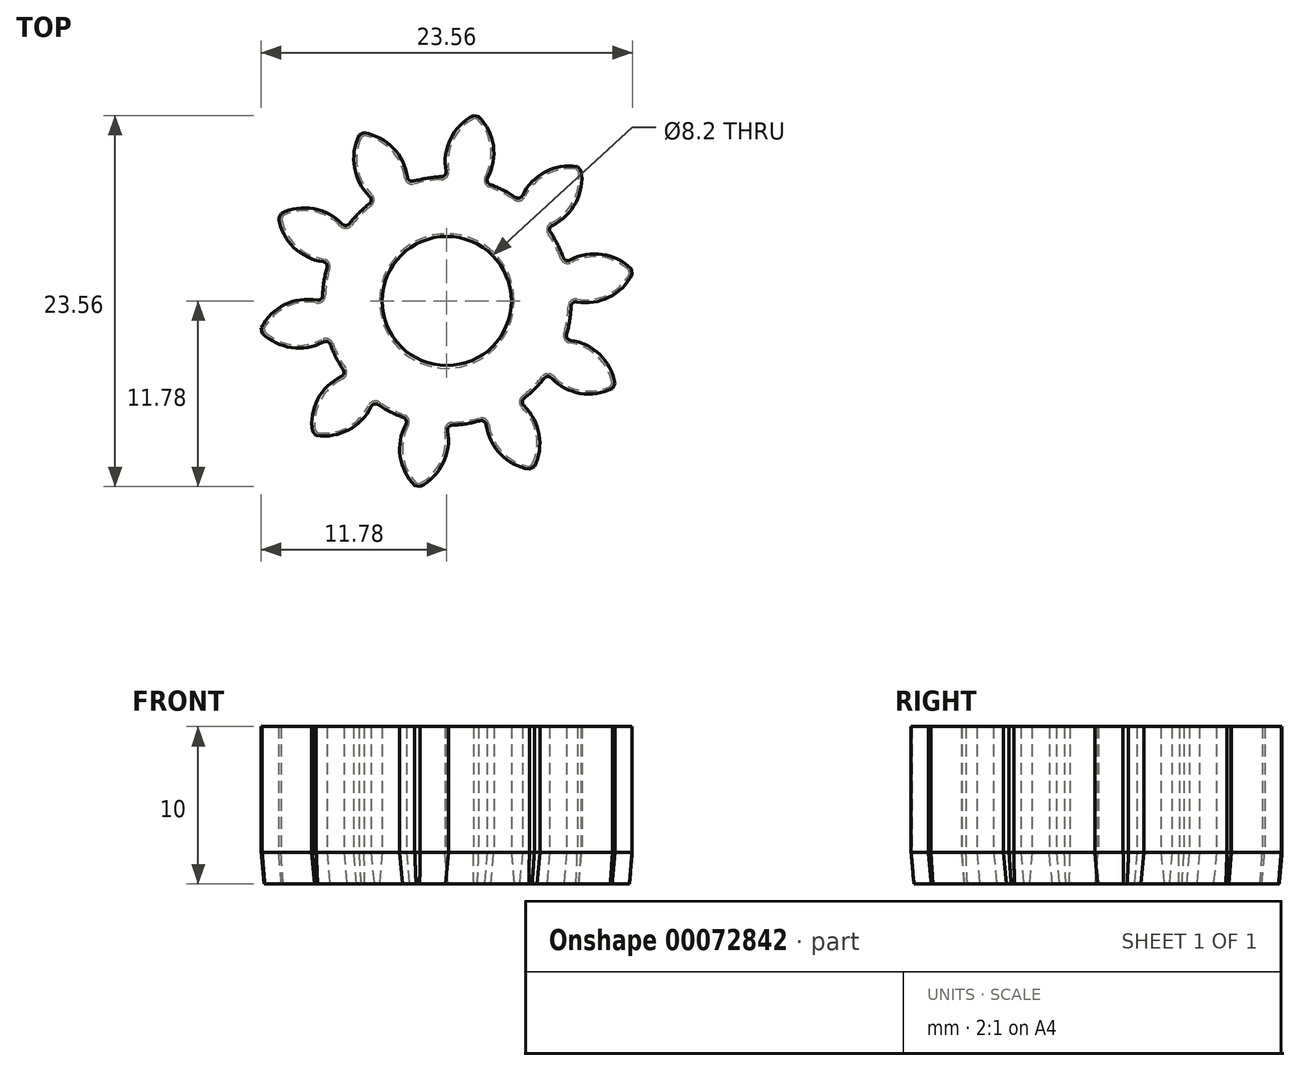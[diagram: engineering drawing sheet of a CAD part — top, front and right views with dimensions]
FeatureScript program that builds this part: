
annotation { "Feature Type Name" : "Feature", "Feature Type Description" : "" }
export const myFeature = defineFeature(function(context is Context, id is Id, definition is map)
    precondition{}
    {
        {
            assignVariable(context, id + "F0", {"name" : "z", "anyValue" : 10});
        }
        {
            assignVariable(context, id + "F1", {"name" : "b1", "anyValue" : 8});
        }
        {
            assignVariable(context, id + "F2", {"name" : "b2", "anyValue" : 2});
        }
        {
            var Q0;
            Q0=qCreatedBy(makeId("Top.planeOp"),FACE);
            var sketch = newSketch(context, id + "F3", { "sketchPlane" : qUnion([Q0])});
            skCircle(sketch, "E0", {"center": v(0, 0) * mm, "radius": 12 * mm, "construction": true});
            skCircle(sketch, "E1", {"center": v(0, 0) * mm, "radius": 9.4 * mm, "construction": true});
            skCircle(sketch, "E2", {"center": v(0, 0) * mm, "radius": 10 * mm, "construction": true});
            skCircle(sketch, "E3", {"center": v(0, 0) * mm, "radius": 8 * mm, "construction": true});
            skLineSegment(sketch, "E4", {"start": v(0, 0) * mm, "end": v(4.1, 11.28) * mm, "construction": true});
            skLineSegment(sketch, "E5", {"start": v(0, 12) * mm, "end": v(0, 0) * mm, "construction": true});
            skCircle(sketch, "E6", {"center": v(3.21, 8.83) * mm, "radius": 3.42 * mm, "construction": true});
            skPoint(sketch, "E7", {"position": v(0, 10) * mm});
            skLineSegment(sketch, "E8", {"start": v(3.7, 11.41) * mm, "end": v(0, 0) * mm, "construction": true});
            skLineSegment(sketch, "E9", {"start": v(0, 0) * mm, "end": v(-0.42, 12) * mm, "construction": true});
            skCircle(sketch, "E10", {"center": v(-0.33, 9.4) * mm, "radius": 3.42 * mm, "construction": true});
            skPoint(sketch, "E11", {"position": v(3.1, 9.51) * mm});
            skCircle(sketch, "E12", {"center": v(0, 0) * mm, "radius": 7.9 * mm, "construction": true});
            skCircle(sketch, "E13", {"center": v(0, 0) * mm, "radius": 11.9 * mm, "construction": true});
            skCircle(sketch, "E14", {"center": v(-0.33, 9.4) * mm, "radius": 3.32 * mm, "construction": true});
            skCircle(sketch, "E15", {"center": v(3.21, 8.83) * mm, "radius": 3.32 * mm, "construction": true});
            skCircle(sketch, "E16", {"center": v(-0.35, 8.2) * mm, "radius": 0.3 * mm, "construction": true});
            skCircle(sketch, "E17", {"center": v(2.86, 7.68) * mm, "radius": 0.3 * mm, "construction": true});
            skPoint(sketch, "E18", {"position": v(-0.34, 7.9) * mm});
            skPoint(sketch, "E19", {"position": v(-0.05, 8.25) * mm});
            skPoint(sketch, "E20", {"position": v(2.6, 7.83) * mm});
            skPoint(sketch, "E21", {"position": v(2.76, 7.4) * mm});
            skPoint(sketch, "E22", {"position": v(2.03, 11.72) * mm});
            skPoint(sketch, "E23", {"position": v(1.69, 11.78) * mm});
            skArc(sketch, "E24", {"start": v(-0.34, 7.9) * mm, "mid": v(-0.12, 8) * mm, "end": v(-0.05, 8.25) * mm});
            skArc(sketch, "E25", {"start": v(1.69, 11.78) * mm, "mid": v(0.24, 10.3) * mm, "end": v(-0.05, 8.25) * mm});
            skArc(sketch, "E26", {"start": v(2.6, 7.83) * mm, "mid": v(2.58, 7.58) * mm, "end": v(2.76, 7.4) * mm});
            skArc(sketch, "E27", {"start": v(2.6, 7.83) * mm, "mid": v(2.96, 9.87) * mm, "end": v(2.03, 11.72) * mm});
            skArc(sketch, "E28", {"start": v(2.76, 7.4) * mm, "mid": v(1.24, 7.8) * mm, "end": v(-0.34, 7.9) * mm});
            skLineSegment(sketch, "E29", {"start": v(2.03, 11.72) * mm, "end": v(1.69, 11.78) * mm});
            skSolve(sketch);
        }
        {
            var Q0;
            Q0 = qSketchRegion(id + "F3", true);
            extrude(context, id + "F4", {"entities" : qUnion([Q0]), "depth" : (getVariable(context, 'b1')) * mm});
        }
        {
            var Q0;
            Q0=qCreatedBy(makeId("Front.planeOp"),FACE);
            var sketch = newSketch(context, id + "F5", { "sketchPlane" : qUnion([Q0])});
            skLineSegment(sketch, "E30", {"start": v(0, 0) * mm, "end": v(0, 12) * mm, "construction": true});
            skSolve(sketch);
        }
        {
            var Q0;
            Q0=makeQuery(id+"F4.opExtrude","SWEPT_BODY",BODY,{"disambiguationData":[OSD([sQuery(id+"F3.wireOp",EDGE,"E24"),sQuery(id+"F3.wireOp",EDGE,"E25"),sQuery(id+"F3.wireOp",EDGE,"E26"),sQuery(id+"F3.wireOp",EDGE,"E27"),sQuery(id+"F3.wireOp",EDGE,"E28"),sQuery(id+"F3.wireOp",EDGE,"debd62c7-c6de-4254-9725-9acab07f6eeb")])]});
            var Q1;
            Q1=sQuery(id+"F5.wireOp",EDGE,"E30");
            circularPattern(context, id + "F6", {"entities" : qUnion([Q0]), "axis" : qUnion([Q1]), "angle" : (360 / getVariable(context, 'z')) * degree, "instanceCount" : getVariable(context, 'z')});
        }
        {
            var Q0;
            Q0=qCreatedBy(makeId("Top.planeOp"),FACE);
            var sketch = newSketch(context, id + "F7", { "sketchPlane" : qUnion([Q0])});
            skCircle(sketch, "E31", {"center": v(0, 0) * mm, "radius": 7.9 * mm});
            skCircle(sketch, "E32", {"center": v(0, 0) * mm, "radius": 4.1 * mm});
            skSolve(sketch);
        }
        {
            var Q0;
            Q0 = qSketchRegion(id + "F7", true);
            extrude(context, id + "F8", {"entities" : qUnion([Q0]), "operationType" : NewBodyOperationType.ADD, "depth" : (getVariable(context, 'b1')) * mm});
        }
        {
            var Q0;
            {var subQ0=makeQuery(id+"F4.opExtrude","CAP_FACE",FACE,{"disambiguationData":[OSD([sQuery(id+"F3.wireOp",EDGE,"E24"),sQuery(id+"F3.wireOp",EDGE,"E25"),sQuery(id+"F3.wireOp",EDGE,"E26"),sQuery(id+"F3.wireOp",EDGE,"E27"),sQuery(id+"F3.wireOp",EDGE,"E28"),sQuery(id+"F3.wireOp",EDGE,"debd62c7-c6de-4254-9725-9acab07f6eeb")])],"isStart":true});Q0=makeQuery(id+"F8.boolean.opBoolean","MERGE",FACE,{"derivedFrom":[subQ0,makeQuery(id+"F6.opPattern","COPY",FACE,{"derivedFrom":subQ0,"instanceName":"1"}),makeQuery(id+"F6.opPattern","COPY",FACE,{"derivedFrom":subQ0,"instanceName":"2"}),makeQuery(id+"F6.opPattern","COPY",FACE,{"derivedFrom":subQ0,"instanceName":"3"}),makeQuery(id+"F6.opPattern","COPY",FACE,{"derivedFrom":subQ0,"instanceName":"4"}),makeQuery(id+"F6.opPattern","COPY",FACE,{"derivedFrom":subQ0,"instanceName":"5"}),makeQuery(id+"F6.opPattern","COPY",FACE,{"derivedFrom":subQ0,"instanceName":"6"}),makeQuery(id+"F6.opPattern","COPY",FACE,{"derivedFrom":subQ0,"instanceName":"7"}),makeQuery(id+"F6.opPattern","COPY",FACE,{"derivedFrom":subQ0,"instanceName":"8"}),makeQuery(id+"F6.opPattern","COPY",FACE,{"derivedFrom":subQ0,"instanceName":"9"}),makeQuery(id+"F6.opPattern","COPY",FACE,{"derivedFrom":subQ0,"instanceName":"10"}),makeQuery(id+"F6.opPattern","COPY",FACE,{"derivedFrom":subQ0,"instanceName":"11"}),makeQuery(id+"F6.opPattern","COPY",FACE,{"derivedFrom":subQ0,"instanceName":"12"}),makeQuery(id+"F6.opPattern","COPY",FACE,{"derivedFrom":subQ0,"instanceName":"13"}),makeQuery(id+"F6.opPattern","COPY",FACE,{"derivedFrom":subQ0,"instanceName":"14"}),makeQuery(id+"F6.opPattern","COPY",FACE,{"derivedFrom":subQ0,"instanceName":"15"}),makeQuery(id+"F6.opPattern","COPY",FACE,{"derivedFrom":subQ0,"instanceName":"16"}),makeQuery(id+"F6.opPattern","COPY",FACE,{"derivedFrom":subQ0,"instanceName":"17"}),makeQuery(id+"F6.opPattern","COPY",FACE,{"derivedFrom":subQ0,"instanceName":"18"}),makeQuery(id+"F6.opPattern","COPY",FACE,{"derivedFrom":subQ0,"instanceName":"19"}),makeQuery(id+"F8.opExtrude","CAP_FACE",FACE,{"disambiguationData":[OSD([sQuery(id+"F7.wireOp",EDGE,"E31"),sQuery(id+"F7.wireOp",EDGE,"E32")])],"isStart":true})]});}
            extrude(context, id + "F9", {"entities" : qUnion([Q0]), "operationType" : NewBodyOperationType.ADD, "depth" : (getVariable(context, 'b2')) * mm, "hasDraft" : true, "draftAngle" : 5 * degree, "draftPullDirection" : true});
        }
    });
